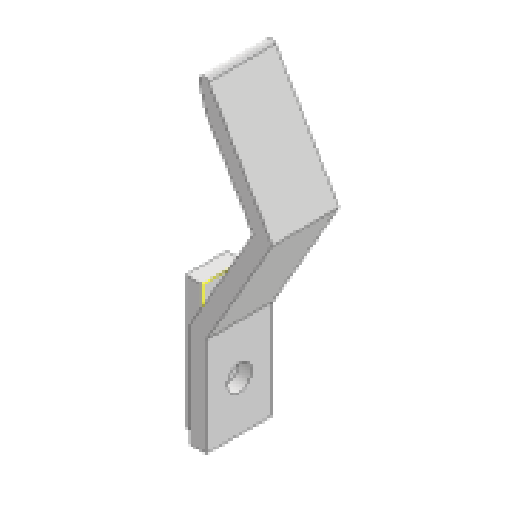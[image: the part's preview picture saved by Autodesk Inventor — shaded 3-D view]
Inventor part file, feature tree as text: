
AUTODESK INVENTOR PART (.ipt)
format: ipt  version: 2025.1 (Build 291241020, 241B)  size: 136,704 bytes
history: native  units: in
note: dims shown in document units (in); Inventor stores cm internally (conversion verified against a paired STEP export)
features: extrude x5, sketch x5, fillet x1, projected_geometry x1
ambient origin geometry x8: Origin, YZ Plane, XZ Plane, XY Plane, X Axis, Y Axis, Z Axis, Center Point
bodies: Solid1 (feature_tree)
feature tree (12):
  extrude  "Extrusion1"  Depth=0.2in
  fillet  "Fillet1"  Radius=0.8in
  extrude  "Extrusion2"  Depth=0.2in
  extrude  "Extrusion3"  TaperAngle=120.0deg  [1 undecoded]
  extrude  "Extrusion4"  Depth=1.525in
  extrude  "Extrusion5"  Depth=0.0625in
  sketch  "Sketch1"  dims[d0=1.238in d1=0.2in d4=0.8in d5=0.0in]
  sketch  "Sketch2"  dims[d6=0.2in d7=0.2in]
  sketch  "Sketch3"  dims[d8=30.0deg d10=120.0deg]
  sketch  "Sketch4"  dims[d11=2.0in d12=1.525in]
  sketch  "Sketch5"  dims[d13=15.0deg d14=0.0625in d15=0.49in d16=1.584in d17=0.245in d18=0.2in d19=0.0in d20=0.14in d21=1.05in d22=0.0in d23=0.3in d24=0.158in d25=0.0in d26=1.0in d27=0.0in]
  projected_geometry  "Projected Loop1"
note: 1 required parameter value undecoded (feature->parameter linkage not recoverable at this tier; creation-order binding heuristic only, values carry confidence <= 0.55)
